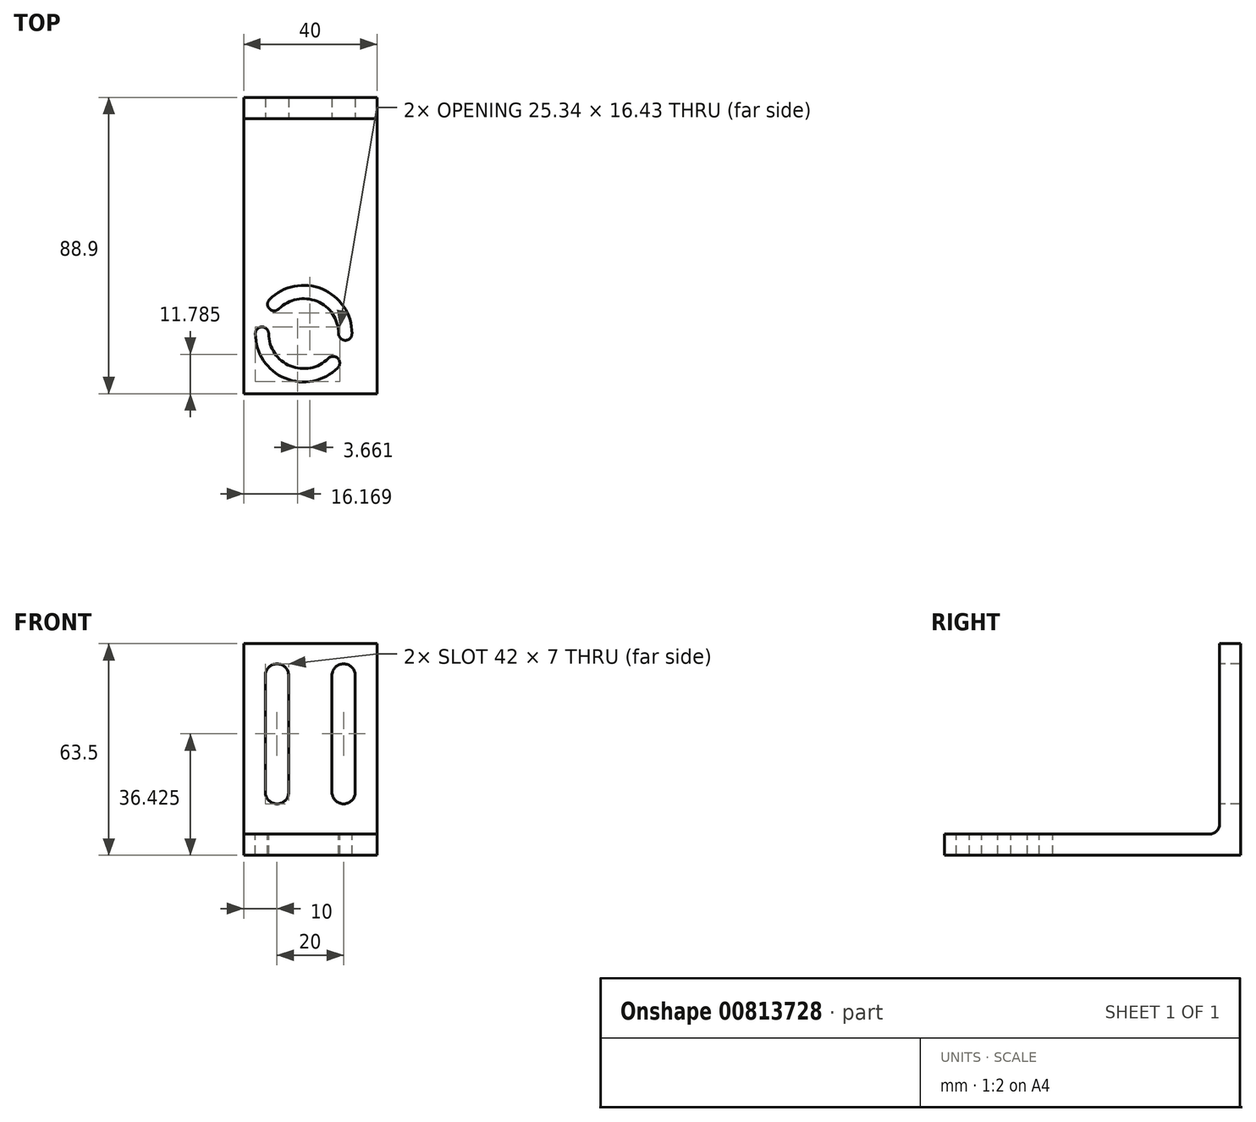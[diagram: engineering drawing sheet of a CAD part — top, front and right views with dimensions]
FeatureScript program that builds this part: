
annotation { "Feature Type Name" : "Feature", "Feature Type Description" : "" }
export const myFeature = defineFeature(function(context is Context, id is Id, definition is map)
    precondition{}
    {
        {
            var Q0;
            Q0=qCreatedBy(makeId("Right.planeOp"),FACE);
            var sketch = newSketch(context, id + "F0", { "sketchPlane" : qUnion([Q0])});
            skLineSegment(sketch, "E0", {"start": v(-44.45, 0) * mm, "end": v(-44.45, 6.35) * mm});
            skLineSegment(sketch, "E1", {"start": v(-44.45, 6.35) * mm, "end": v(38.1, 6.35) * mm});
            skLineSegment(sketch, "E2", {"start": v(44.45, 63.5) * mm, "end": v(38.1, 63.5) * mm});
            skLineSegment(sketch, "E3", {"start": v(-44.45, 0) * mm, "end": v(44.45, 0) * mm});
            skLineSegment(sketch, "E4", {"start": v(44.45, 63.5) * mm, "end": v(44.45, 0) * mm});
            skLineSegment(sketch, "E5", {"start": v(38.1, 63.5) * mm, "end": v(38.1, 6.35) * mm});
            skSolve(sketch);
        }
        {
            var Q0;
            Q0 = qSketchRegion(id + "F0", true);
            extrude(context, id + "F1", {"entities" : qUnion([Q0]), "depth" : 40 * mm, "offsetDistance" : 25 * mm});
        }
        {
            var Q0;
            Q0=makeQuery(id+"F1.opExtrude","SWEPT_FACE",FACE,{"disambiguationData":[OSD([sQuery(id+"F0.wireOp",EDGE,"E1")])]});
            var Q1;
            Q1=makeQuery(id+"F1.opExtrude","SWEPT_FACE",FACE,{"disambiguationData":[OSD([sQuery(id+"F0.wireOp",EDGE,"E1")])]});
            var sketch = newSketch(context, id + "F2", { "sketchPlane" : qUnion([Q0, Q1])});
            skArc(sketch, "E6", {"start": v(5.5, -26.45) * mm, "mid": v(13.22, -38) * mm, "end": v(26.84, -35.29) * mm});
            skLineSegment(sketch, "E7", {"start": v(9.16, -17.61) * mm, "end": v(26.84, -35.29) * mm, "construction": true});
            skLineSegment(sketch, "E8", {"start": v(18, -38.95) * mm, "end": v(18, -13.95) * mm, "construction": true});
            skLineSegment(sketch, "E9", {"start": v(5.5, -26.45) * mm, "end": v(30.5, -26.45) * mm, "construction": true});
            skLineSegment(sketch, "E10", {"start": v(9.16, -35.29) * mm, "end": v(26.84, -17.61) * mm, "construction": true});
            skArc(sketch, "E11.trimOffspring", {"start": v(30.5, -26.45) * mm, "mid": v(22.78, -14.9) * mm, "end": v(9.16, -17.61) * mm});
            skArc(sketch, "E12.0.startCap", {"start": v(3.5, -26.45) * mm, "mid": v(5.5, -24.45) * mm, "end": v(7.5, -26.45) * mm});
            skArc(sketch, "E12.0.endCap", {"start": v(25.42, -33.87) * mm, "mid": v(28.25, -33.87) * mm, "end": v(28.25, -36.7) * mm});
            skArc(sketch, "E12.0.left", {"start": v(7.5, -26.45) * mm, "mid": v(13.98, -36.15) * mm, "end": v(25.42, -33.87) * mm});
            skArc(sketch, "E12.0.right", {"start": v(3.5, -26.45) * mm, "mid": v(12.45, -39.85) * mm, "end": v(28.25, -36.7) * mm});
            skArc(sketch, "E12.1.startCap", {"start": v(32.5, -26.45) * mm, "mid": v(30.5, -28.45) * mm, "end": v(28.5, -26.45) * mm});
            skArc(sketch, "E12.1.endCap", {"start": v(10.58, -19.03) * mm, "mid": v(7.75, -19.03) * mm, "end": v(7.75, -16.2) * mm});
            skArc(sketch, "E12.1.left", {"start": v(28.5, -26.45) * mm, "mid": v(22.02, -16.75) * mm, "end": v(10.58, -19.03) * mm});
            skArc(sketch, "E12.1.right", {"start": v(32.5, -26.45) * mm, "mid": v(23.55, -13.05) * mm, "end": v(7.75, -16.2) * mm});
            skSolve(sketch);
        }
        {
            var Q0;
            Q0 = qSketchRegion(id + "F2", true);
            extrude(context, id + "F3", {"entities" : qUnion([Q0]), "operationType" : NewBodyOperationType.REMOVE, "oppositeDirection" : true, "depth" : 25 * mm, "offsetDistance" : 25 * mm});
        }
        {
            var Q0;
            Q0=makeQuery(id+"F1.opExtrude","SWEPT_EDGE",EDGE,{"disambiguationData":[OSD([sQuery(id+"F0.wireOp",EDGE,"E1"),sQuery(id+"F0.wireOp",EDGE,"E5")])]});
            fillet(context, id + "F4", {"entities" : qUnion([Q0]), "radius" : 3 * mm, "tangentPropagation" : true, "allowEdgeOverflow" : false});
        }
        {
            var Q0;
            Q0=makeQuery(id+"F1.opExtrude","SWEPT_FACE",FACE,{"disambiguationData":[OSD([sQuery(id+"F0.wireOp",EDGE,"E5")])]});
            var sketch = newSketch(context, id + "F5", { "sketchPlane" : qUnion([Q0])});
            skLineSegment(sketch, "E13.bottom", {"start": v(10, 53.92) * mm, "end": v(30, 53.92) * mm, "construction": true});
            skLineSegment(sketch, "E13.top", {"start": v(10, 18.92) * mm, "end": v(30, 18.92) * mm, "construction": true});
            skLineSegment(sketch, "E13.left", {"start": v(10, 53.92) * mm, "end": v(10, 18.92) * mm});
            skLineSegment(sketch, "E13.right", {"start": v(30, 53.92) * mm, "end": v(30, 18.92) * mm});
            skLineSegment(sketch, "E14", {"start": v(0, 36.42) * mm, "end": v(10, 36.42) * mm, "construction": true});
            skArc(sketch, "E15.0.startCap", {"start": v(6.5, 53.92) * mm, "mid": v(10, 57.43) * mm, "end": v(13.5, 53.92) * mm});
            skArc(sketch, "E15.0.endCap", {"start": v(13.5, 18.92) * mm, "mid": v(10, 15.42) * mm, "end": v(6.5, 18.92) * mm});
            skLineSegment(sketch, "E15.0.left", {"start": v(13.5, 53.92) * mm, "end": v(13.5, 18.92) * mm});
            skLineSegment(sketch, "E15.0.right", {"start": v(6.5, 53.92) * mm, "end": v(6.5, 18.92) * mm});
            skArc(sketch, "E15.1.startCap", {"start": v(26.5, 53.92) * mm, "mid": v(30, 57.43) * mm, "end": v(33.5, 53.92) * mm});
            skArc(sketch, "E15.1.endCap", {"start": v(33.5, 18.92) * mm, "mid": v(30, 15.42) * mm, "end": v(26.5, 18.92) * mm});
            skLineSegment(sketch, "E15.1.left", {"start": v(33.5, 53.92) * mm, "end": v(33.5, 18.92) * mm});
            skLineSegment(sketch, "E15.1.right", {"start": v(26.5, 53.92) * mm, "end": v(26.5, 18.92) * mm});
            skSolve(sketch);
        }
        {
            var Q0;
            Q0 = qSketchRegion(id + "F5", true);
            extrude(context, id + "F6", {"entities" : qUnion([Q0]), "operationType" : NewBodyOperationType.REMOVE, "oppositeDirection" : true, "depth" : 25 * mm, "offsetDistance" : 25 * mm});
        }
    });
